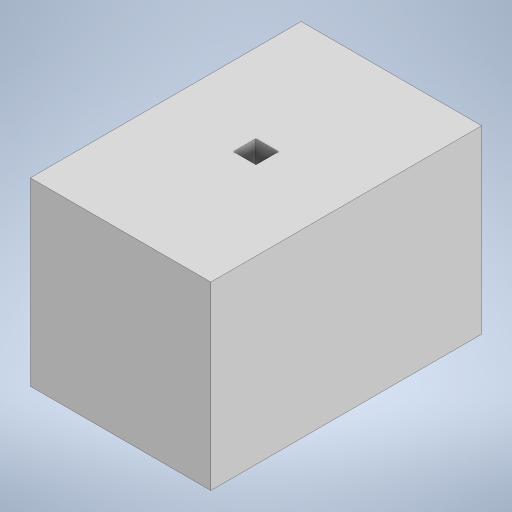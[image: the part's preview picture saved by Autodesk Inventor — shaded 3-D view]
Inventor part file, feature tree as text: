
AUTODESK INVENTOR PART (.ipt)
format: ipt  version: 2024 (Build 280153000, 153)  size: 187,392 bytes
history: native  units: in
note: dims shown in document units (in); Inventor stores cm internally (conversion verified against a paired STEP export)
features: extrude x1, sketch x1
ambient origin geometry x8: Origin, YZ Plane, XZ Plane, XY Plane, X Axis, Y Axis, Z Axis, Center Point
bodies: Solid1 (feature_tree)
feature tree (2):
  extrude  "Extrusion1"  Depth=3.1496in
  sketch  "Sketch1"  dims[d1=4.7244in d2=3.1496in d3=0.3937in d4=0.3937in d5=0.1969in d6=0.1969in d7=1.5748in d8=2.3622in d9=3.1496in d10=0.0in d11=0.5in d12=0.0344in d13=0.5in d14=0.0344in]
